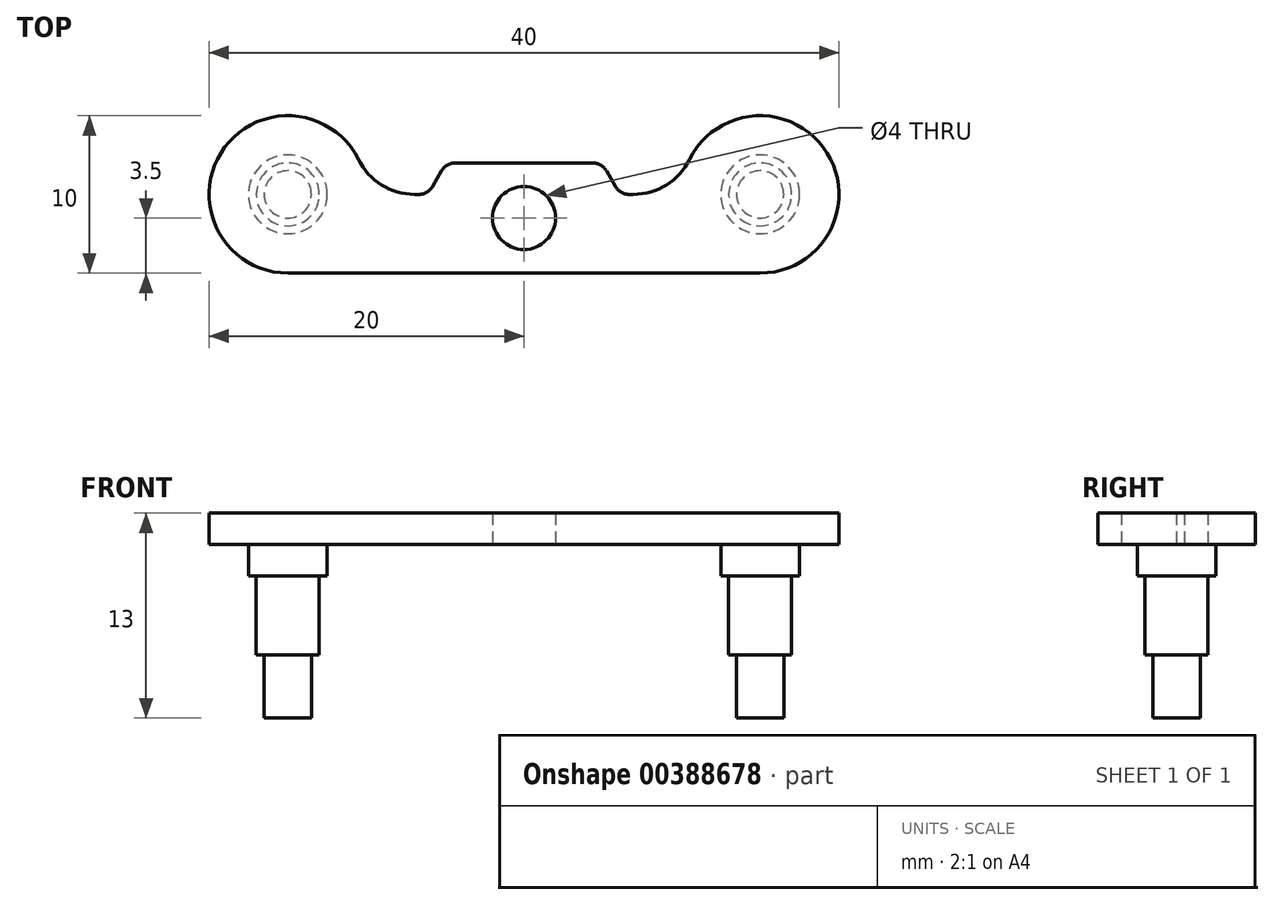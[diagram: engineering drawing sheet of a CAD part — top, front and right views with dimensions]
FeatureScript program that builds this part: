
annotation { "Feature Type Name" : "Feature", "Feature Type Description" : "" }
export const myFeature = defineFeature(function(context is Context, id is Id, definition is map)
    precondition{}
    {
        {
            var Q0;
            Q0=qCreatedBy(makeId("Top.planeOp"),FACE);
            var sketch = newSketch(context, id + "F0", { "sketchPlane" : qUnion([Q0])});
            skLineSegment(sketch, "E0", {"start": v(0, -5) * mm, "end": v(30, -5) * mm});
            skLineSegment(sketch, "E1", {"start": v(30, -5) * mm, "end": v(30, 0) * mm, "construction": true});
            skLineSegment(sketch, "E2", {"start": v(30, 0) * mm, "end": v(25, 0) * mm, "construction": true});
            skLineSegment(sketch, "E3", {"start": v(0, 0) * mm, "end": v(0, -5) * mm, "construction": true});
            skCircle(sketch, "E4", {"center": v(0, 0) * mm, "radius": 6.5 * mm, "construction": true});
            skCircle(sketch, "E5", {"center": v(30, 0) * mm, "radius": 6.5 * mm, "construction": true});
            skLineSegment(sketch, "E6", {"start": v(5, 0) * mm, "end": v(0, 0) * mm, "construction": true});
            skArc(sketch, "E7", {"start": v(0, -5) * mm, "mid": v(3.54, -3.54) * mm, "end": v(5, 0) * mm, "construction": true});
            skArc(sketch, "E8", {"start": v(4.48, 2.22) * mm, "mid": v(-4.25, 2.64) * mm, "end": v(0, -5) * mm});
            skLineSegment(sketch, "E9", {"start": v(21.94, 0) * mm, "end": v(21.67, 0) * mm});
            skArc(sketch, "E10", {"start": v(25, 0) * mm, "mid": v(26.46, -3.54) * mm, "end": v(30, -5) * mm, "construction": true});
            skArc(sketch, "E11", {"start": v(30, -5) * mm, "mid": v(34.25, 2.64) * mm, "end": v(25.52, 2.22) * mm});
            skPoint(sketch, "E12.visualSharp", {"position": v(5, 0) * mm});
            skArc(sketch, "E12.filletArc", {"start": v(4.48, 2.22) * mm, "mid": v(5.95, 0.6) * mm, "end": v(8.06, 0) * mm});
            skPoint(sketch, "E13.visualSharp", {"position": v(25, 0) * mm});
            skArc(sketch, "E13.filletArc", {"start": v(21.94, 0) * mm, "mid": v(24.05, 0.6) * mm, "end": v(25.52, 2.22) * mm});
            skPoint(sketch, "E14", {"position": v(15, -1.5) * mm});
            skLineSegment(sketch, "E15", {"start": v(10.64, 2) * mm, "end": v(19.36, 2) * mm});
            skLineSegment(sketch, "E16", {"start": v(20.23, 1.5) * mm, "end": v(20.8, 0.5) * mm});
            skLineSegment(sketch, "E17", {"start": v(9.77, 1.5) * mm, "end": v(9.2, 0.5) * mm});
            skLineSegment(sketch, "E18.trimOffspring", {"start": v(8.33, 0) * mm, "end": v(8.06, 0) * mm});
            skPoint(sketch, "E19.visualSharp", {"position": v(10.06, 2) * mm});
            skArc(sketch, "E19.filletArc", {"start": v(10.64, 2) * mm, "mid": v(10.14, 1.87) * mm, "end": v(9.77, 1.5) * mm});
            skPoint(sketch, "E20.visualSharp", {"position": v(19.94, 2) * mm});
            skArc(sketch, "E20.filletArc", {"start": v(20.23, 1.5) * mm, "mid": v(19.86, 1.87) * mm, "end": v(19.36, 2) * mm});
            skPoint(sketch, "E21.visualSharp", {"position": v(21.1, 0) * mm});
            skArc(sketch, "E21.filletArc", {"start": v(20.8, 0.5) * mm, "mid": v(21.17, 0.13) * mm, "end": v(21.67, 0) * mm});
            skPoint(sketch, "E22.visualSharp", {"position": v(8.9, 0) * mm});
            skArc(sketch, "E22.filletArc", {"start": v(8.33, 0) * mm, "mid": v(8.83, 0.13) * mm, "end": v(9.2, 0.5) * mm});
            skPoint(sketch, "E23", {"position": v(15, 2) * mm});
            skLineSegment(sketch, "E24", {"start": v(15, 2) * mm, "end": v(15, -5) * mm, "construction": true});
            skSolve(sketch);
        }
        {
            var Q0;
            Q0 = qSketchRegion(id + "F0", true);
            extrude(context, id + "F1", {"entities" : qUnion([Q0]), "depth" : 2 * mm});
        }
        {
            var Q0;
            Q0=qCreatedBy(makeId("Top.planeOp"),FACE);
            var sketch = newSketch(context, id + "F2", { "sketchPlane" : qUnion([Q0])});
            skCircle(sketch, "E25", {"center": v(0, 0) * mm, "radius": 2.5 * mm});
            skPoint(sketch, "E26.0", {"position": v(30, 0) * mm});
            skCircle(sketch, "E27", {"center": v(30, 0) * mm, "radius": 2.5 * mm});
            skSolve(sketch);
        }
        {
            var Q0;
            Q0 = qSketchRegion(id + "F2", true);
            extrude(context, id + "F3", {"entities" : qUnion([Q0]), "operationType" : NewBodyOperationType.ADD, "oppositeDirection" : true, "depth" : 2 * mm});
        }
        {
            var Q0;
            Q0=qCreatedBy(makeId("Top.planeOp"),FACE);
            var sketch = newSketch(context, id + "F4", { "sketchPlane" : qUnion([Q0])});
            skCircle(sketch, "E28", {"center": v(0, 0) * mm, "radius": 2 * mm});
            skPoint(sketch, "E29.0", {"position": v(30, 0) * mm});
            skCircle(sketch, "E30", {"center": v(30, 0) * mm, "radius": 2 * mm});
            skSolve(sketch);
        }
        {
            var Q0;
            Q0 = qSketchRegion(id + "F4", true);
            extrude(context, id + "F5", {"entities" : qUnion([Q0]), "operationType" : NewBodyOperationType.ADD, "oppositeDirection" : true, "depth" : 7 * mm});
        }
        {
            var Q0;
            Q0=qCreatedBy(makeId("Top.planeOp"),FACE);
            var sketch = newSketch(context, id + "F6", { "sketchPlane" : qUnion([Q0])});
            skCircle(sketch, "E31", {"center": v(0, 0) * mm, "radius": 1.5 * mm});
            skPoint(sketch, "E32.0", {"position": v(30, 0) * mm});
            skCircle(sketch, "E33", {"center": v(30, 0) * mm, "radius": 1.5 * mm});
            skSolve(sketch);
        }
        {
            var Q0;
            Q0 = qSketchRegion(id + "F6", true);
            extrude(context, id + "F7", {"entities" : qUnion([Q0]), "operationType" : NewBodyOperationType.ADD, "oppositeDirection" : true, "depth" : 11 * mm});
        }
        {
            var Q0;
            Q0=sQuery(id+"F0.wireOp",VERTEX,"7bfd22ed-b761-40cf-ae7f-8a51215b8e9e");
            var Q1;
            Q1=sQuery(id+"F0.wireOp",VERTEX,"E14");
            var Q2;
            Q2=makeQuery(id+"F1.opExtrude","SWEPT_BODY",BODY,{"disambiguationData":[OSD([sQuery(id+"F0.wireOp",EDGE,"E0"),sQuery(id+"F0.wireOp",EDGE,"E8"),sQuery(id+"F0.wireOp",EDGE,"E9"),sQuery(id+"F0.wireOp",EDGE,"E11"),sQuery(id+"F0.wireOp",EDGE,"E12.filletArc"),sQuery(id+"F0.wireOp",EDGE,"E13.filletArc")])]});
            hole(context, id + "F8", {"style" : HoleStyle.SIMPLE, "endStyle" : HoleEndStyle.THROUGH, "oppositeDirection" : true, "standardTappedOrClearance" : lookupTablePath({ "standard" : "ISO", "size" : "4", "type" : "Drilled" }), "standardBlindInLast" : lookupTablePath({ "standard" : "ISO", "size" : "4", "type" : "Drilled" }), "holeDiameter" : 4 * mm, "isTappedThrough" : true, "tappedDepth" : 12 * mm, "tapClearance" : 3, "locations" : qUnion([Q0, Q1]), "scope" : qUnion([Q2])});
        }
    });
